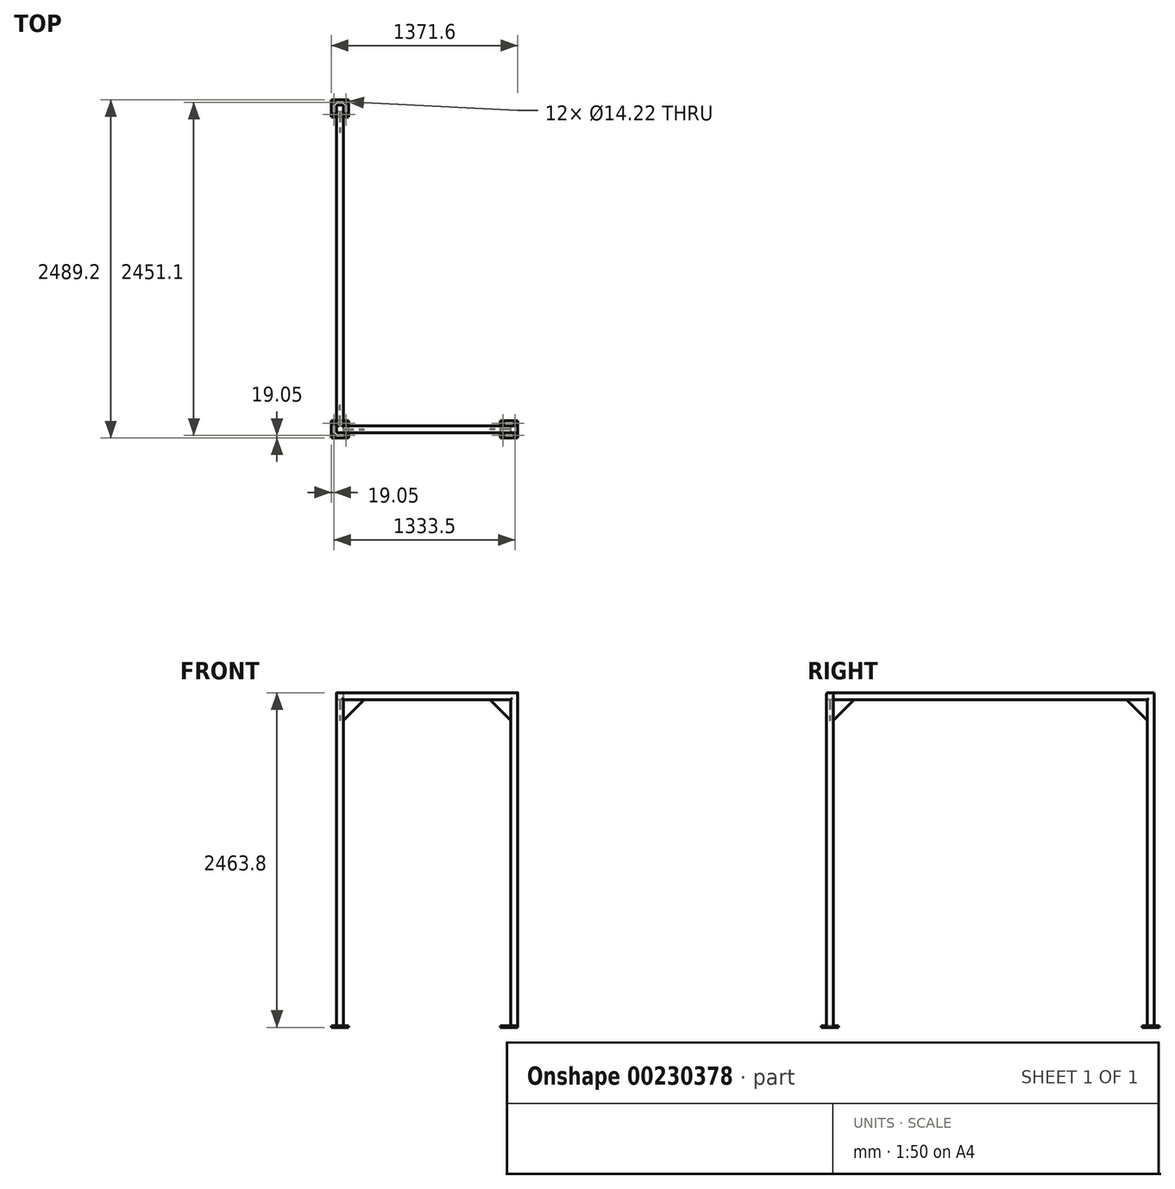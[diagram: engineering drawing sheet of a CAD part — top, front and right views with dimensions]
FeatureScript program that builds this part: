
annotation { "Feature Type Name" : "Feature", "Feature Type Description" : "" }
export const myFeature = defineFeature(function(context is Context, id is Id, definition is map)
    precondition{}
    {
        {
            var Q0;
            Q0=qCreatedBy(makeId("Right.planeOp"),FACE);
            var sketch = newSketch(context, id + "F0", { "sketchPlane" : qUnion([Q0])});
            skLineSegment(sketch, "E0", {"start": v(0, 0) * mm, "end": v(0, 2438.4) * mm});
            skLineSegment(sketch, "E1", {"start": v(0, 2438.4) * mm, "end": v(2362.2, 2438.4) * mm});
            skLineSegment(sketch, "E2", {"start": v(2362.2, 2438.4) * mm, "end": v(2362.2, 0) * mm});
            skSolve(sketch);
        }
        {
            var Q0;
            Q0=qCreatedBy(makeId("Top.planeOp"),FACE);
            var sketch = newSketch(context, id + "F1", { "sketchPlane" : qUnion([Q0])});
            skLineSegment(sketch, "E3.bottom", {"start": v(-15.88, 25.4) * mm, "end": v(15.88, 25.4) * mm});
            skLineSegment(sketch, "E3.top", {"start": v(-15.88, -25.4) * mm, "end": v(15.87, -25.4) * mm});
            skLineSegment(sketch, "E3.left", {"start": v(-25.4, 15.88) * mm, "end": v(-25.4, -15.87) * mm});
            skLineSegment(sketch, "E3.right", {"start": v(25.4, 15.88) * mm, "end": v(25.4, -15.88) * mm});
            skPoint(sketch, "E3.middle", {"position": v(0, 0) * mm});
            skPoint(sketch, "E4.visualSharp", {"position": v(-25.4, -25.4) * mm});
            skArc(sketch, "E4.filletArc", {"start": v(-25.4, -15.87) * mm, "mid": v(-22.61, -22.61) * mm, "end": v(-15.88, -25.4) * mm});
            skPoint(sketch, "E5.visualSharp", {"position": v(-25.4, 25.4) * mm});
            skArc(sketch, "E5.filletArc", {"start": v(-15.88, 25.4) * mm, "mid": v(-22.61, 22.61) * mm, "end": v(-25.4, 15.88) * mm});
            skPoint(sketch, "E6.visualSharp", {"position": v(25.4, 25.4) * mm});
            skArc(sketch, "E6.filletArc", {"start": v(25.4, 15.88) * mm, "mid": v(22.61, 22.61) * mm, "end": v(15.88, 25.4) * mm});
            skPoint(sketch, "E7.visualSharp", {"position": v(25.4, -25.4) * mm});
            skArc(sketch, "E7.filletArc", {"start": v(15.87, -25.4) * mm, "mid": v(22.61, -22.61) * mm, "end": v(25.4, -15.88) * mm});
            skPoint(sketch, "E8.0", {"position": v(0, 1181.1) * mm});
            skLineSegment(sketch, "E9.0", {"start": v(0, 0) * mm, "end": v(0, 2362.2) * mm});
            skPoint(sketch, "E10.0.1.0", {"position": v(0, 2362.2) * mm});
            skLineSegment(sketch, "E10.0.1.1", {"start": v(-15.88, 2387.6) * mm, "end": v(15.88, 2387.6) * mm});
            skLineSegment(sketch, "E10.0.1.2", {"start": v(-25.4, 2378.08) * mm, "end": v(-25.4, 2346.33) * mm});
            skLineSegment(sketch, "E10.0.1.3", {"start": v(25.4, 2378.08) * mm, "end": v(25.4, 2346.33) * mm});
            skPoint(sketch, "E10.0.1.4", {"position": v(-25.4, 2336.8) * mm});
            skPoint(sketch, "E10.0.1.5", {"position": v(25.4, 2336.8) * mm});
            skPoint(sketch, "E10.0.1.6", {"position": v(25.4, 2387.6) * mm});
            skPoint(sketch, "E10.0.1.7", {"position": v(-25.4, 2387.6) * mm});
            skLineSegment(sketch, "E10.0.1.8", {"start": v(-15.88, 2336.8) * mm, "end": v(15.87, 2336.8) * mm});
            skArc(sketch, "E10.0.1.9", {"start": v(-25.4, 2346.33) * mm, "mid": v(-22.61, 2339.59) * mm, "end": v(-15.88, 2336.8) * mm});
            skArc(sketch, "E10.0.1.10", {"start": v(-15.88, 2387.6) * mm, "mid": v(-22.61, 2384.81) * mm, "end": v(-25.4, 2378.07) * mm});
            skArc(sketch, "E10.0.1.11", {"start": v(25.4, 2378.07) * mm, "mid": v(22.61, 2384.81) * mm, "end": v(15.88, 2387.6) * mm});
            skArc(sketch, "E10.0.1.12", {"start": v(15.87, 2336.8) * mm, "mid": v(22.61, 2339.59) * mm, "end": v(25.4, 2346.33) * mm});
            skLineSegment(sketch, "E10.direction1", {"start": v(-25.4, -25.4) * mm, "end": v(0, -25.4) * mm, "construction": true});
            skLineSegment(sketch, "E10.direction2", {"start": v(-25.4, -25.4) * mm, "end": v(-25.4, 2336.8) * mm, "construction": true});
            skSolve(sketch);
        }
        {
            var Q0;
            Q0=qCreatedBy(makeId("Front.planeOp"),FACE);
            var sketch = newSketch(context, id + "F2", { "sketchPlane" : qUnion([Q0])});
            skLineSegment(sketch, "E11.0", {"start": v(0, 2438.4) * mm, "end": v(0, 0) * mm});
            skLineSegment(sketch, "E12", {"start": v(0, 2438.4) * mm, "end": v(1282.7, 2438.4) * mm});
            skLineSegment(sketch, "E13", {"start": v(1282.7, 2438.4) * mm, "end": v(1282.7, 0) * mm});
            skSolve(sketch);
        }
        {
            var Q0;
            Q0=makeQuery(id+"F1.imprint","IMPRINT",FACE,{"disambiguationData":[TD([[makeQuery(id+"F1.imprint","IMPRINT",EDGE,{"derivedFrom":sQuery(id+"F1.wireOp",EDGE,"E3.bottom")}),-1.0]])]});
            var Q1;
            Q1=sQuery(id+"F2.wireOp",EDGE,"E11.0");
            var Q2;
            Q2=sQuery(id+"F2.wireOp",EDGE,"E12");
            var Q3;
            Q3=sQuery(id+"F2.wireOp",EDGE,"E13");
            sweep(context, id + "F3", {"profiles" : qUnion([Q0]), "path" : qUnion([Q1, Q2, Q3])});
        }
        {
            var Q0;
            Q0=makeQuery(id+"F1.imprint","IMPRINT",FACE,{"disambiguationData":[TD([[makeQuery(id+"F1.imprint","IMPRINT",EDGE,{"derivedFrom":sQuery(id+"F1.wireOp",EDGE,"E10.0.1.1")}),-1.0]])]});
            var Q1;
            Q1=sQuery(id+"F0.wireOp",EDGE,"E2");
            var Q2;
            Q2=sQuery(id+"F0.wireOp",EDGE,"E1");
            sweep(context, id + "F4", {"operationType" : NewBodyOperationType.ADD, "profiles" : qUnion([Q0]), "path" : qUnion([Q1, Q2])});
        }
        {
            var Q0;
            Q0=qCreatedBy(makeId("Top.planeOp"),FACE);
            var sketch = newSketch(context, id + "F5", { "sketchPlane" : qUnion([Q0])});
            skLineSegment(sketch, "E14.bottom", {"start": v(63.5, -63.5) * mm, "end": v(-63.5, -63.5) * mm});
            skLineSegment(sketch, "E14.top", {"start": v(63.5, 63.5) * mm, "end": v(-63.5, 63.5) * mm});
            skLineSegment(sketch, "E14.left", {"start": v(63.5, -63.5) * mm, "end": v(63.5, 63.5) * mm});
            skLineSegment(sketch, "E14.right", {"start": v(-63.5, -63.5) * mm, "end": v(-63.5, 63.5) * mm});
            skPoint(sketch, "E14.middle", {"position": v(0, 0) * mm});
            skLineSegment(sketch, "E15.0", {"start": v(44.45, -44.45) * mm, "end": v(44.45, 44.45) * mm, "construction": true});
            skLineSegment(sketch, "E15.1", {"start": v(44.45, -44.45) * mm, "end": v(-44.45, -44.45) * mm, "construction": true});
            skLineSegment(sketch, "E15.2", {"start": v(-44.45, -44.45) * mm, "end": v(-44.45, 44.45) * mm, "construction": true});
            skLineSegment(sketch, "E15.3", {"start": v(44.45, 44.45) * mm, "end": v(-44.45, 44.45) * mm, "construction": true});
            skCircle(sketch, "E16", {"center": v(44.45, -44.45) * mm, "radius": 7.11 * mm});
            skCircle(sketch, "E17.0.1.0", {"center": v(44.45, 44.45) * mm, "radius": 7.11 * mm});
            skCircle(sketch, "E17.1.0.0", {"center": v(-44.45, -44.45) * mm, "radius": 7.11 * mm});
            skCircle(sketch, "E17.1.1.0", {"center": v(-44.45, 44.45) * mm, "radius": 7.11 * mm});
            skPoint(sketch, "E18.0.1.0", {"position": v(0, 2362.2) * mm});
            skLineSegment(sketch, "E18.0.1.1", {"start": v(63.5, 2298.7) * mm, "end": v(63.5, 2425.7) * mm});
            skLineSegment(sketch, "E18.0.1.2", {"start": v(-63.5, 2298.7) * mm, "end": v(-63.5, 2425.7) * mm});
            skLineSegment(sketch, "E18.0.1.3", {"start": v(63.5, 2425.7) * mm, "end": v(-63.5, 2425.7) * mm});
            skLineSegment(sketch, "E18.0.1.4", {"start": v(-44.45, 2317.75) * mm, "end": v(-44.45, 2406.65) * mm, "construction": true});
            skLineSegment(sketch, "E18.0.1.5", {"start": v(44.45, 2406.65) * mm, "end": v(-44.45, 2406.65) * mm, "construction": true});
            skLineSegment(sketch, "E18.0.1.6", {"start": v(44.45, 2317.75) * mm, "end": v(-44.45, 2317.75) * mm, "construction": true});
            skLineSegment(sketch, "E18.0.1.7", {"start": v(44.45, 2317.75) * mm, "end": v(44.45, 2406.65) * mm, "construction": true});
            skLineSegment(sketch, "E18.0.1.8", {"start": v(63.5, 2298.7) * mm, "end": v(-63.5, 2298.7) * mm});
            skLineSegment(sketch, "E18.0.1.9", {"start": v(44.45, 2317.75) * mm, "end": v(-44.45, 2317.75) * mm, "construction": true});
            skLineSegment(sketch, "E18.0.1.10", {"start": v(44.45, 2317.75) * mm, "end": v(44.45, 2406.65) * mm, "construction": true});
            skCircle(sketch, "E18.0.1.11", {"center": v(-44.45, 2406.65) * mm, "radius": 7.11 * mm});
            skCircle(sketch, "E18.0.1.12", {"center": v(44.45, 2406.65) * mm, "radius": 7.11 * mm});
            skCircle(sketch, "E18.0.1.13", {"center": v(-44.45, 2317.75) * mm, "radius": 7.11 * mm});
            skCircle(sketch, "E18.0.1.14", {"center": v(44.45, 2317.75) * mm, "radius": 7.11 * mm});
            skPoint(sketch, "E18.1.0.0", {"position": v(1244.6, 0) * mm});
            skLineSegment(sketch, "E18.1.0.1", {"start": v(1308.1, -63.5) * mm, "end": v(1308.1, 63.5) * mm});
            skLineSegment(sketch, "E18.1.0.2", {"start": v(1181.1, -63.5) * mm, "end": v(1181.1, 63.5) * mm});
            skLineSegment(sketch, "E18.1.0.3", {"start": v(1308.1, 63.5) * mm, "end": v(1181.1, 63.5) * mm});
            skLineSegment(sketch, "E18.1.0.4", {"start": v(1200.15, -44.45) * mm, "end": v(1200.15, 44.45) * mm, "construction": true});
            skLineSegment(sketch, "E18.1.0.5", {"start": v(1289.05, 44.45) * mm, "end": v(1200.15, 44.45) * mm, "construction": true});
            skLineSegment(sketch, "E18.1.0.6", {"start": v(1289.05, -44.45) * mm, "end": v(1200.15, -44.45) * mm, "construction": true});
            skLineSegment(sketch, "E18.1.0.7", {"start": v(1289.05, -44.45) * mm, "end": v(1289.05, 44.45) * mm, "construction": true});
            skLineSegment(sketch, "E18.1.0.8", {"start": v(1308.1, -63.5) * mm, "end": v(1181.1, -63.5) * mm});
            skLineSegment(sketch, "E18.1.0.9", {"start": v(1289.05, -44.45) * mm, "end": v(1200.15, -44.45) * mm, "construction": true});
            skLineSegment(sketch, "E18.1.0.10", {"start": v(1289.05, -44.45) * mm, "end": v(1289.05, 44.45) * mm, "construction": true});
            skCircle(sketch, "E18.1.0.11", {"center": v(1200.15, 44.45) * mm, "radius": 7.11 * mm});
            skCircle(sketch, "E18.1.0.12", {"center": v(1289.05, 44.45) * mm, "radius": 7.11 * mm});
            skCircle(sketch, "E18.1.0.13", {"center": v(1200.15, -44.45) * mm, "radius": 7.11 * mm});
            skCircle(sketch, "E18.1.0.14", {"center": v(1289.05, -44.45) * mm, "radius": 7.11 * mm});
            skLineSegment(sketch, "E18.direction1", {"start": v(-63.5, -63.5) * mm, "end": v(1181.1, -63.5) * mm, "construction": true});
            skLineSegment(sketch, "E18.direction2", {"start": v(-63.5, -63.5) * mm, "end": v(-63.5, 2298.7) * mm, "construction": true});
            skSolve(sketch);
        }
        {
            var Q0;
            Q0 = qSketchRegion(id + "F5", true);
            extrude(context, id + "F6", {"entities" : qUnion([Q0]), "operationType" : NewBodyOperationType.ADD, "depth" : 12.7 * mm});
        }
        {
            var Q0;
            Q0=qCreatedBy(makeId("Right.planeOp"),FACE);
            var sketch = newSketch(context, id + "F7", { "sketchPlane" : qUnion([Q0])});
            skLineSegment(sketch, "E19.0", {"start": v(2336.8, 12.7) * mm, "end": v(2336.8, 2413) * mm, "construction": true});
            skLineSegment(sketch, "E20.0", {"start": v(2336.8, 2413) * mm, "end": v(25.4, 2413) * mm, "construction": true});
            skLineSegment(sketch, "E21.0", {"start": v(25.4, 12.7) * mm, "end": v(25.4, 2413) * mm, "construction": true});
            skLineSegment(sketch, "E22.bottom", {"start": v(2336.8, 2413) * mm, "end": v(2184.4, 2413) * mm});
            skLineSegment(sketch, "E22.top", {"start": v(2336.8, 2260.6) * mm, "end": v(2184.4, 2260.6) * mm});
            skLineSegment(sketch, "E22.left", {"start": v(2336.8, 2413) * mm, "end": v(2336.8, 2260.6) * mm});
            skLineSegment(sketch, "E23.bottom", {"start": v(25.4, 2413) * mm, "end": v(177.8, 2413) * mm});
            skLineSegment(sketch, "E23.top", {"start": v(25.4, 2260.6) * mm, "end": v(177.8, 2260.6) * mm});
            skLineSegment(sketch, "E23.left", {"start": v(25.4, 2413) * mm, "end": v(25.4, 2260.6) * mm});
            skLineSegment(sketch, "E24", {"start": v(2336.8, 2260.6) * mm, "end": v(2184.4, 2413) * mm});
            skLineSegment(sketch, "E25", {"start": v(177.8, 2413) * mm, "end": v(25.4, 2260.6) * mm});
            skSolve(sketch);
        }
        {
            var Q0;
            Q0 = qSketchRegion(id + "F7", true);
            extrude(context, id + "F8", {"entities" : qUnion([Q0]), "operationType" : NewBodyOperationType.ADD, "endBound" : BoundingType.SYMMETRIC, "depth" : 6.35 * mm});
        }
        {
            var Q0;
            Q0=qCreatedBy(makeId("Front.planeOp"),FACE);
            var sketch = newSketch(context, id + "F9", { "sketchPlane" : qUnion([Q0])});
            skLineSegment(sketch, "E26.0", {"start": v(25.4, 12.7) * mm, "end": v(25.4, 2413) * mm, "construction": true});
            skLineSegment(sketch, "E27.0", {"start": v(25.4, 2413) * mm, "end": v(1257.3, 2413) * mm, "construction": true});
            skLineSegment(sketch, "E28.0", {"start": v(1257.3, 2413) * mm, "end": v(1257.3, 12.7) * mm, "construction": true});
            skLineSegment(sketch, "E29.bottom", {"start": v(25.4, 2413) * mm, "end": v(177.8, 2413) * mm});
            skLineSegment(sketch, "E29.top", {"start": v(25.4, 2260.6) * mm, "end": v(177.8, 2260.6) * mm});
            skLineSegment(sketch, "E29.left", {"start": v(25.4, 2413) * mm, "end": v(25.4, 2260.6) * mm});
            skPoint(sketch, "E30.oppositeSnap0", {"position": v(101.6, 2260.6) * mm});
            skLineSegment(sketch, "E30.bottom", {"start": v(1257.3, 2413) * mm, "end": v(1104.9, 2413) * mm});
            skLineSegment(sketch, "E30.top", {"start": v(1257.3, 2260.6) * mm, "end": v(1104.9, 2260.6) * mm});
            skLineSegment(sketch, "E30.left", {"start": v(1257.3, 2413) * mm, "end": v(1257.3, 2260.6) * mm});
            skLineSegment(sketch, "E31", {"start": v(25.4, 2260.6) * mm, "end": v(177.8, 2413) * mm});
            skLineSegment(sketch, "E32", {"start": v(1104.9, 2413) * mm, "end": v(1257.3, 2260.6) * mm});
            skSolve(sketch);
        }
        {
            var Q0;
            Q0 = qSketchRegion(id + "F9", true);
            extrude(context, id + "F10", {"entities" : qUnion([Q0]), "operationType" : NewBodyOperationType.ADD, "endBound" : BoundingType.SYMMETRIC, "depth" : 6.35 * mm});
        }
    });
